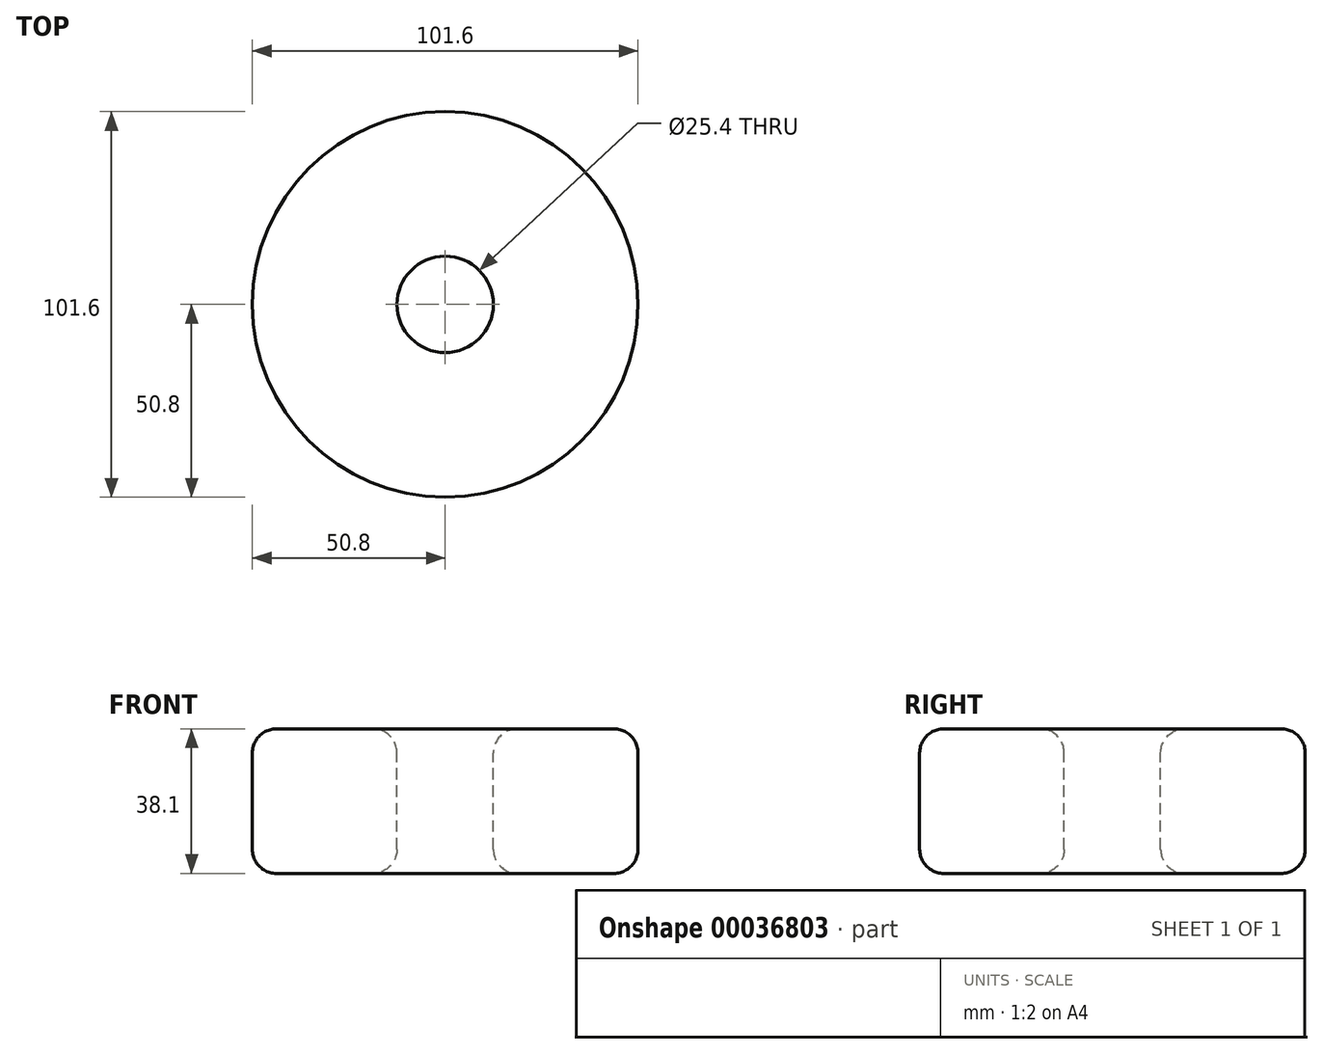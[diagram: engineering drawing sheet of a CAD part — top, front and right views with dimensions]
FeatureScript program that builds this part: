
annotation { "Feature Type Name" : "Feature", "Feature Type Description" : "" }
export const myFeature = defineFeature(function(context is Context, id is Id, definition is map)
    precondition{}
    {
        {
            var Q0;
            Q0=qCreatedBy(makeId("Front.planeOp"),FACE);
            var sketch = newSketch(context, id + "F0", { "sketchPlane" : qUnion([Q0])});
            skLineSegment(sketch, "E0.bottom", {"start": v(19.05, 0) * mm, "end": v(44.45, 0) * mm});
            skLineSegment(sketch, "E0.top", {"start": v(19.05, 38.1) * mm, "end": v(44.45, 38.1) * mm});
            skLineSegment(sketch, "E0.left", {"start": v(12.7, 6.35) * mm, "end": v(12.7, 31.75) * mm});
            skLineSegment(sketch, "E0.right", {"start": v(50.8, 6.35) * mm, "end": v(50.8, 31.75) * mm});
            skPoint(sketch, "E1.visualSharp", {"position": v(12.7, 38.1) * mm});
            skArc(sketch, "E1.filletArc", {"start": v(19.05, 38.1) * mm, "mid": v(14.56, 36.24) * mm, "end": v(12.7, 31.75) * mm});
            skPoint(sketch, "E2.visualSharp", {"position": v(50.8, 38.1) * mm});
            skArc(sketch, "E2.filletArc", {"start": v(50.8, 31.75) * mm, "mid": v(48.94, 36.24) * mm, "end": v(44.45, 38.1) * mm});
            skPoint(sketch, "E3.visualSharp", {"position": v(50.8, 0) * mm});
            skArc(sketch, "E3.filletArc", {"start": v(44.45, 0) * mm, "mid": v(48.94, 1.86) * mm, "end": v(50.8, 6.35) * mm});
            skPoint(sketch, "E4.visualSharp", {"position": v(12.7, 0) * mm});
            skArc(sketch, "E4.filletArc", {"start": v(12.7, 6.35) * mm, "mid": v(14.56, 1.86) * mm, "end": v(19.05, 0) * mm});
            skSolve(sketch);
        }
        {
            var Q0;
            Q0=qCreatedBy(makeId("Top.planeOp"),FACE);
            cPlane(context, id + "F1", {"entities" : qUnion([Q0]), "cplaneType" : CPlaneType.OFFSET, "offset" : 19.05 * mm, "width" : 152.4 * mm, "height" : 152.4 * mm});
        }
        {
            var Q0;
            Q0=qCreatedBy(id+"F1.planeOp",FACE);
            var sketch = newSketch(context, id + "F2", { "sketchPlane" : qUnion([Q0])});
            skCircle(sketch, "E5", {"center": v(0, 0) * mm, "radius": 25.4 * mm});
            skSolve(sketch);
        }
        {
            var Q0;
            Q0 = qSketchRegion(id + "F0", true);
            var Q1;
            Q1 = qConstructionFilter(qBodyType(qCreatedBy(id + "F2" ,EDGE), BodyType.WIRE), ConstructionObject.NO);
            sweep(context, id + "F3", {"profiles" : qUnion([Q0]), "path" : qUnion([Q1])});
        }
    });
